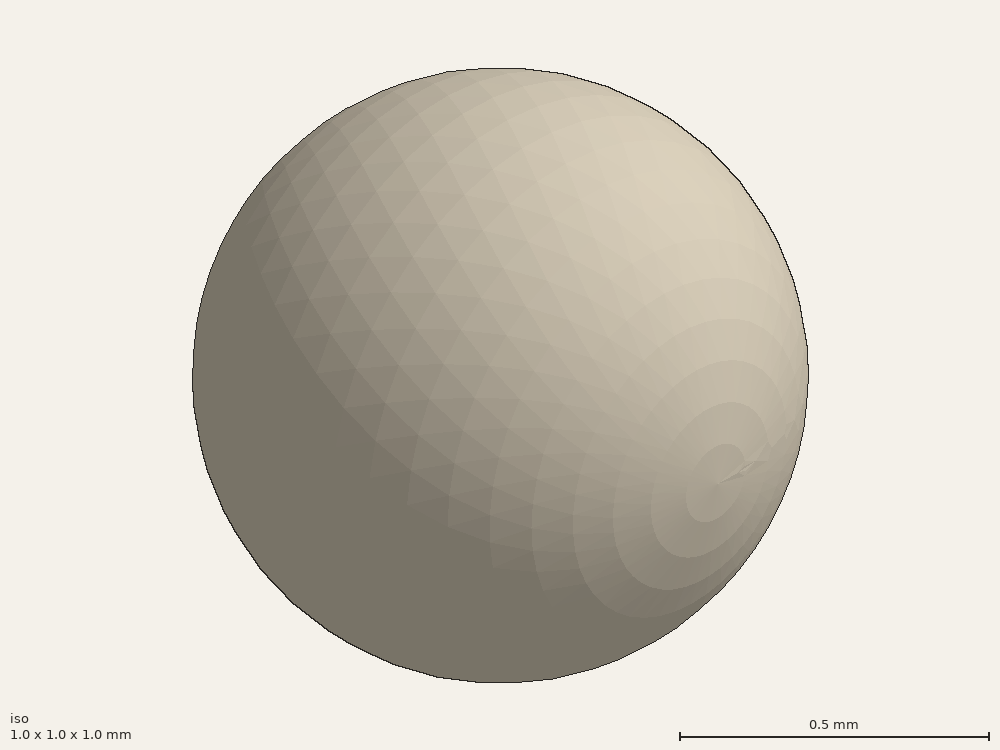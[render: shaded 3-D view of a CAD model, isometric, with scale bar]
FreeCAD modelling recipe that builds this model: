
FCSTD DOCUMENT  (FreeCAD 0.19R)
Label: sphere
License: All rights reserved
LicenseURL: http://en.wikipedia.org/wiki/All_rights_reserved
objects: Sketcher::SketchObject×1, PartDesign::Revolution×1, PartDesign::Body×1
note: 4 computed .brp shape members not serialized (recipe doc carries the construction recipe); baked Part::Feature solids carry a one-line shape summary decoded from their .brp

FEATURE [Sketcher::SketchObject] Sketch
  FullyConstrained = true
  MapMode = 5
  Support = -> [XY_Plane]
  sketch-geometry (2):
    g0: ArcOfCircle CenterX=0 CenterY=0 CenterZ=0 NormalX=0 NormalY=0 NormalZ=1 AngleXU=0 Radius=0.5 StartAngle=4.71239 EndAngle=7.85398
    g1: LineSegment StartX=2e-16 StartY=0.5 StartZ=0 EndX=-1e-16 EndY=-0.5 EndZ=0
  constraints (6):
    c: Coincident(g0,g-1)
    c: PointOnObject(g0,g-2)
    c: PointOnObject(g0,g-2)
    c: Radius(g0) = 0.5
    c: Coincident(g1,g0)
    c: Coincident(g1,g0)
FEATURE [PartDesign::Revolution] Revolution
  Angle = 360
  Axis = (0,1,0)
  Base = (0,0,0)
  Profile = -> Sketch
  ReferenceAxis = -> Sketch [V_Axis]
  Reversed = true
FEATURE [PartDesign::Body] Body
  Group = -> [Sketch,Revolution]
  Origin = -> Origin
  Tip = -> Revolution
